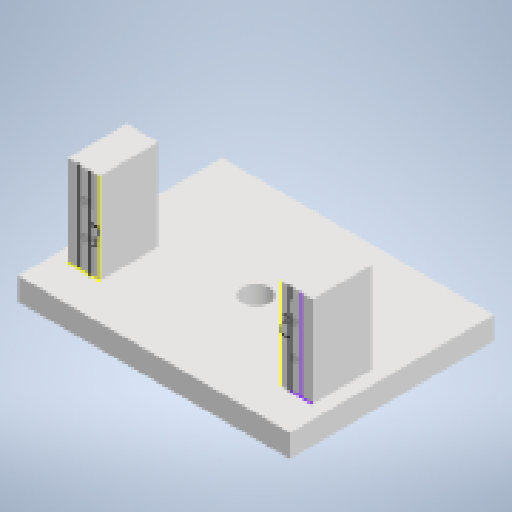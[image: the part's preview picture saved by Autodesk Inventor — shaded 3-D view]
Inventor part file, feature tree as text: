
AUTODESK INVENTOR PART (.ipt)
format: ipt  version: 2025.2 (Build 292293000, 293)  size: 301,056 bytes
history: native  units: in
note: dims shown in document units (in); Inventor stores cm internally (conversion verified against a paired STEP export)
features: sketch x7, extrude x6, thread x4
ambient origin geometry x8: Origin, YZ Plane, XZ Plane, XY Plane, X Axis, Y Axis, Z Axis, Center Point
bodies: Solid1 (feature_tree)
feature tree (17):
  extrude  "Extrusion1"  Depth=1.7717in
  extrude  "Extrusion2"  Depth=0.1969in TaperAngle=0.0deg
  extrude  "Extrusion3"  Depth=0.3937in TaperAngle=0.0deg
  extrude  "Extrusion5"  Depth=0.315in
  sketch  "Sketch7"  dims[d24=1.063in d25=0.5118in d26=0.2756in d27=0.5118in d28=0.2756in d29=0.7874in d30=0.0in]
  extrude  "Extrusion6"  Depth=0.5118in
  thread  "Thread1"  [1 undecoded]
  thread  "Thread2"  [1 undecoded]
  thread  "Thread3"  [1 undecoded]
  thread  "Thread4"  [1 undecoded]
  extrude  "Extrusion7"  Depth=0.0787in
  sketch  "Sketch1"  dims[d2=2.3622in d3=1.7717in]
  sketch  "Sketch2"  dims[d4=0.1969in d5=0.0in d7=0.4724in d8=0.0in]
  sketch  "Sketch3"  dims[d9=0.3937in d10=0.3937in d11=0.0in]
  sketch  "Sketch6"  dims[d22=0.315in d23=1.063in]
  sketch  "Sketch8"  dims[d31=0.0787in d32=0.0787in]
  sketch  "Sketch9"  dims[d43=0.5512in d44=0.0in d45=0.5118in d46=0.0in d47=0.5118in d48=0.0in d49=0.5118in d50=0.0in d51=0.5118in d52=0.0in d53=1.5748in d54=0.0in d55=0.0197in d56=0.0344in]
note: 4 required parameter values undecoded (feature->parameter linkage not recoverable at this tier; creation-order binding heuristic only, values carry confidence <= 0.55)
